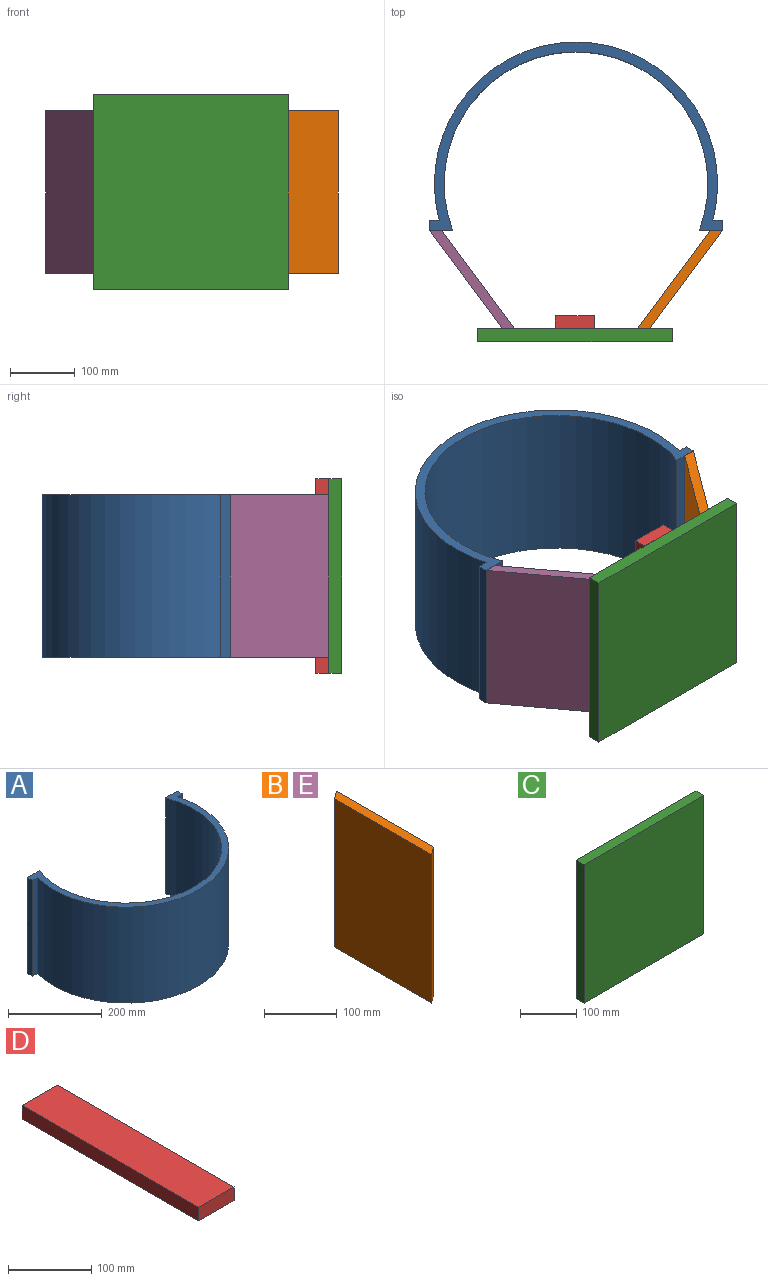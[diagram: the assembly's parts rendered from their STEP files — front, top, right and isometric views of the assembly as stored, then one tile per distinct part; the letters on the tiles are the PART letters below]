
ASSEMBLY  parts=5 mates=4
PART A: 10 faces, bbox 451.5x289.8x250 mm
  f0: plane 250x15mm, normal (0,-1,0), area 3750mm2, adj f1,f7,f8,f9
  f1: cylinder r=218.2mm len=436.4mm, axis (0,0,-1), area 200001.3mm2, adj f0,f2,f8,f9
  f2: plane 250x15mm, normal (0,-1,0), area 3750mm2, adj f1,f3,f8,f9
  f3: plane 250x15mm, normal (1,0,0), area 3750mm2, adj f2,f4,f8,f9
  f4: plane 250x35.56mm, normal (0,1,0), area 8890.9mm2, adj f3,f5,f8,f9
  f5: cylinder r=203.2mm len=406.4mm, axis (0,0,-1), area 196178.5mm2, adj f4,f6,f8,f9
  f6: plane 250x35.56mm, normal (0,1,0), area 8890.9mm2, adj f5,f7,f8,f9
  f7: plane 250x15mm, normal (-1,0,0), area 3750mm2, adj f0,f6,f8,f9
  f8: plane 451.46x289.8mm, normal (0,0,1), area 12637mm2, adj f0,f1,f2,f3,f4,f5,f6,f7
  f9: plane 451.46x289.8mm, normal (0,0,-1), area 12637mm2, adj f0,f1,f2,f3,f4,f5,f6,f7
PART B: 6 faces, bbox 15x200x250 mm
  f0: plane 250x188.9mm, normal (-1,0,0), area 47225.1mm2, adj f1,f2,f4,f5
  f1: plane 200x15mm, normal (0,0,-1), area 2833.5mm2, adj f0,f3,f4,f5
  f2: plane 200x15mm, normal (0,0,1), area 2833.5mm2, adj f0,f3,f4,f5
  f3: plane 250x188.9mm, normal (1,0,0), area 47225.1mm2, adj f1,f2,f4,f5
  f4: plane 250x15mm, normal (0.59,-0.8,0), area 4665mm2, adj f0,f1,f2,f3
  f5: plane 250x15mm, normal (-0.59,0.8,0), area 4665mm2, adj f0,f1,f2,f3
PART C: 6 faces, bbox 300x20x300 mm
  f0: plane 300x20mm, normal (1,0,0), area 6000mm2, adj f1,f3,f4,f5
  f1: plane 300x20mm, normal (0,0,1), area 6000mm2, adj f0,f2,f4,f5
  f2: plane 300x20mm, normal (-1,0,0), area 6000mm2, adj f1,f3,f4,f5
  f3: plane 300x20mm, normal (0,0,-1), area 6000mm2, adj f0,f2,f4,f5
  f4: plane 300x300mm, normal (0,-1,0), area 90000mm2, adj f0,f1,f2,f3
  f5: plane 300x300mm, normal (0,1,0), area 90000mm2, adj f0,f1,f2,f3
PART D: 6 faces, bbox 60x300x20 mm
  f0: plane 300x20mm, normal (1,0,0), area 6000mm2, adj f1,f3,f4,f5
  f1: plane 60x20mm, normal (0,1,0), area 1200mm2, adj f0,f2,f4,f5
  f2: plane 300x20mm, normal (-1,0,0), area 6000mm2, adj f1,f3,f4,f5
  f3: plane 60x20mm, normal (0,-1,0), area 1200mm2, adj f0,f2,f4,f5
  f4: plane 300x60mm, normal (0,0,1), area 18000mm2, adj f0,f1,f2,f3
  f5: plane 300x60mm, normal (0,0,-1), area 18000mm2, adj f0,f1,f2,f3
PART E: same geometry as B
PLACE A rot(axis=(0,0,-1),180deg) t=(125.02,-424.97,0)mm
PLACE B rot(axis=(0,0,1),143.5deg) t=(291.26,-576.96,125)mm
PLACE C t=(123.38,-648.42,125)mm
PLACE D rot(axis=(-1,0,0),90deg) t=(123.38,-648.42,125)mm
PLACE E rot(axis=(0.31,-0.95,0),180deg) t=(-29.18,-568.03,125)mm
MATE fastened D.f5 <-> C.f5  axis (0,-1,0) through (123.38,-648.42,275)mm
MATE fastened E.f5 <-> A.f4  axis (0,1,0) through (-100.72,-496.57,125)mm
MATE fastened B.f4 <-> A.f6  axis (0,1,0) through (350.75,-496.57,125)mm
MATE fastened C.f5 <-> B.f5  axis (0,1,0) through (273.38,-648.42,125)mm
